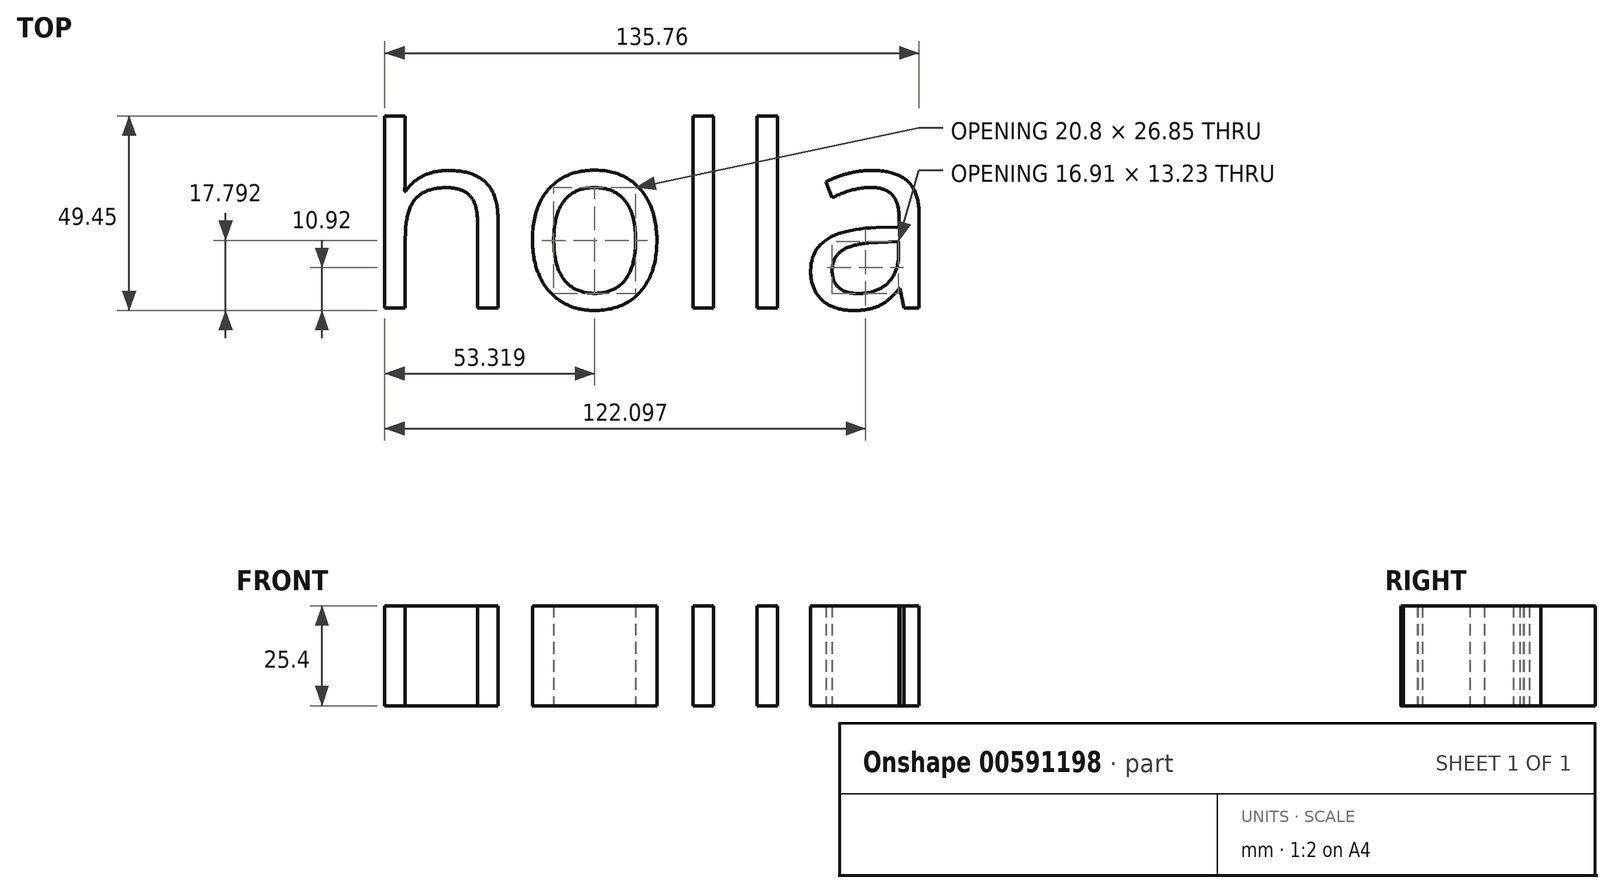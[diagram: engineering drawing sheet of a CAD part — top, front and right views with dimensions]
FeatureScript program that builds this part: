
annotation { "Feature Type Name" : "Feature", "Feature Type Description" : "" }
export const myFeature = defineFeature(function(context is Context, id is Id, definition is map)
    precondition{}
    {
        {
            var Q0;
            Q0=qCreatedBy(makeId("Top.planeOp"),FACE);
            var sketch = newSketch(context, id + "F0", { "sketchPlane" : qUnion([Q0])});
            skLineSegment(sketch, "E0", {"start": v(-71.38, 54.7) * mm, "end": v(76.31, -74.8) * mm});
            skText(sketch, "E1", { "text": "holla\n", "fontName": "OpenSans-Regular.ttf"});
            const initialGuessF0  = {"E1": [-0.06835, -0.0308, 1, 0, 0.04626]};
            skSetInitialGuess(sketch, initialGuessF0);
            skSolve(sketch);
        }
        {
            var Q0;
            Q0 = qSketchRegion(id + "F0", true);
            extrude(context, id + "F1", {"entities" : qUnion([Q0]), "depth" : 25.4 * mm, "offsetDistance" : 25.4 * mm});
        }
    });
